# Revit family: Sanitary_Installation-Systems_AXOR_12676XXX-AXOR-Starck-Basic-set-for-showe
name_source: partatom
category: Plumbing Fixtures
revit_build: Autodesk Revit 2018 (Build: 20190510_1515(x64)
units: mm (PartAtom-declared; Revit-internal decimal feet)

## family parameters
Cut with Voids When Loaded = Yes
Host = Face
OmniClass Number = 23.31.17.29
OmniClass Title = Shower Drains
Part Type = Normal
Room Calculation Point = No
Round Connector Dimension = Use Diameter
Shared = No

## types (1)
- 12676XXX AXOR Starck Basic set for shower panel
    BIMobject category = Installation Systems
    Connector Description = Water Inlet 19.05 mm
    Default Elevation = 1219.2 mm  [stored 4 ft]
    Description = AXOR Starck Basic set for shower panel
    Design country = Germany
    Diameter = 19.05 mm  [stored 0.0625 ft]
    Edition number = 1
    IFC Classification = Pipe Fitting
    Manufacturer = AXOR
    Manufacturer country = Germany
    Manufacturer name = AXOR
    Masterformat 2014 Code = 22 41 39
    Masterformat 2014 Description = Residential Faucets, Supplies, and Trim
    Material 1 = AXOR - Metal - Stainless Steel
    Material 2 = AXOR - Plastic - Green
    Material 3 = AXOR - Metal - Brass
    Material 4 = AXOR - Plastic - White
    Material 5 = AXOR - Plastic - Black
    Material 6 = AXOR - Plastic - Gray
    Model = 12676XXX
    OmniClass Code = 23-27 31 29 15
    OmniClass Description = Thermostatically Controlled Mixing Valves
    Product Guid = 9c6957ff-9a74-4473-80ee-b3ef3b75cd60
    Product SKU = 12676XXX
    Product data url = https://bimobject.com
    Product family = AXOR Starck
    Product group = Shower columns
    Product name = 12676XXX AXOR Starck Basic set for shower panel
    Product url = https://www.axor-design.com
    QR code = https://bimobject.com
    UNSPSC Code = 30181503
    URL = https://www.axor-design.com
    Uniclass 2015 Code = Pr_65_54_95_88
    Uniclass 2015 Name = Thermostatic mixing valves
    Uniformat II Code = D2010
    Uniformat II Description = Plumbing Fixtures
    Version = 0

note: [stored X ft] marks values corroborated as IEEE doubles in the binary element streams (Revit-internal decimal feet)

## geometry (parser evidence)
native form markers: Sweep x2
no freeform markers — native parametric forms only
